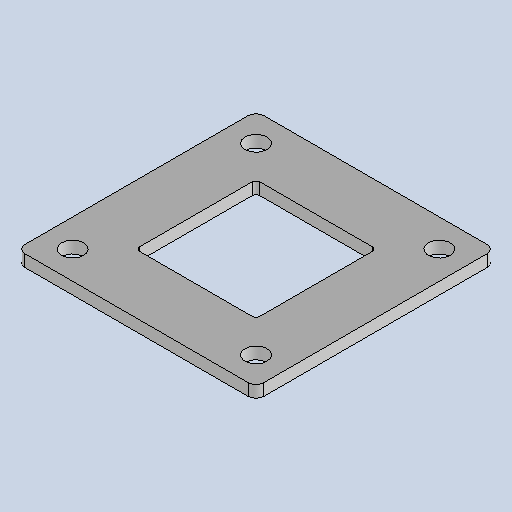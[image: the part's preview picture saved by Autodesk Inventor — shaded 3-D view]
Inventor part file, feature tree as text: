
AUTODESK INVENTOR PART (.ipt)
format: ipt  version: 2025.3 (Build 293356030, 356C)  size: 218,624 bytes
history: native  units: mm
features: chamfer x2, other x2, sheet_metal_op x1, sketch x1
ambient origin geometry x8: Origin, YZ Plane, XZ Plane, XY Plane, X Axis, Y Axis, Z Axis, Center Point
bodies: Body1 (feature_tree)
feature tree (6):
  sheet_metal_op  "Face3"
  chamfer  "Corner Round1"
  chamfer  "Corner Round2"
  sketch  "Sketch1"  dims[d156=3.0mm d172=30.2mm d178=2.0mm d179=1.0mm d190=5.5mm d191=46.0mm d192=60.0mm]
  other  "Plate5"
  other  "Definition1"
